# Revit family: AQ0029_Profil sous plafond PRENIUM
name_source: partatom
category: Portes
units: mm (PartAtom-declared; Revit-internal decimal feet)

## family parameters
Couper avec des vides une fois chargée = Non
Hôte = Mur
Numéro OmniClass = 23.30.10.00
Partagée = Non
Repère de localisation dans la pièce = Non
Titre OmniClass = Doors
Toujours verticalement = Oui

## types (1)
- AQ0029_Profil sous plafond PRENIUM
    Construction analytique = <Aucun>
    Decalage_Boite_Elec = 200 mm
    Dim_Boit_Elec_Longueur = 400 mm
    Dim_Boite_Elec_Largeur = 400 mm
    Définir les propriétés thermiques par = Type schématique
    Ebrasement = 20 mm
    Fermeture du mur = Par hôte
    Fonction = Intérieur
    Haut_Volet_Roulant = 391 mm
    Hauteur_Boite_Elec = 1000 mm
    Hauteur_Ouverture_Porte = 1300 mm  [stored 4.26509 ft]
    Hauteur_Volet = 342 mm
    Largeur du cadre = 75 mm
    Largeur_Montant_Industrie = 160 mm
    Profondeur_Montant_Industrie = 95 mm
    Projection - Ext. de l'encadrement = 25 mm
    Projection Int. de l'encadrement = 25 mm

note: [stored X ft] marks values corroborated as IEEE doubles in the binary element streams (Revit-internal decimal feet)
